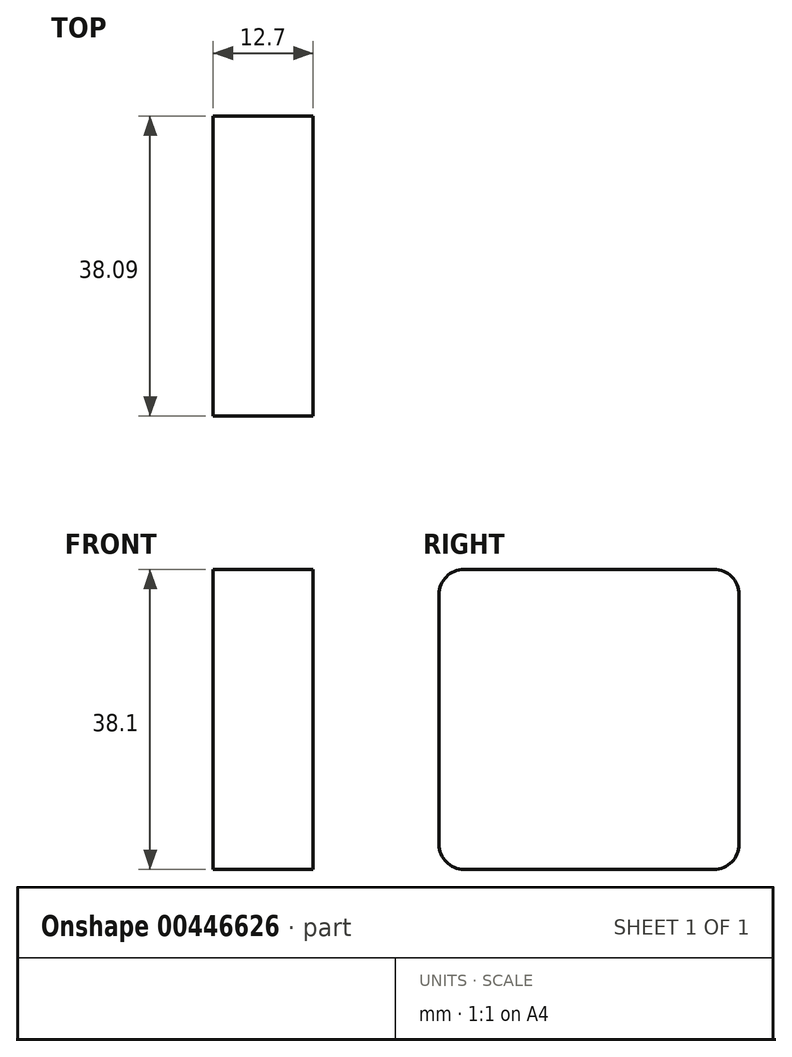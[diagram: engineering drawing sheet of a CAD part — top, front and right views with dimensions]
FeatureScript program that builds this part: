
annotation { "Feature Type Name" : "Feature", "Feature Type Description" : "" }
export const myFeature = defineFeature(function(context is Context, id is Id, definition is map)
    precondition{}
    {
        {
            var Q0;
            Q0=qCreatedBy(makeId("Right.planeOp"),FACE);
            var sketch = newSketch(context, id + "F0", { "sketchPlane" : qUnion([Q0])});
            skLineSegment(sketch, "E0.0", {"start": v(34.93, 0) * mm, "end": v(34.93, 31.75) * mm});
            skLineSegment(sketch, "E0.1", {"start": v(0, -3.17) * mm, "end": v(31.75, -3.17) * mm});
            skLineSegment(sketch, "E0.2", {"start": v(-3.18, 0) * mm, "end": v(-3.18, 31.75) * mm});
            skLineSegment(sketch, "E0.3", {"start": v(0, 34.93) * mm, "end": v(31.75, 34.93) * mm});
            skPoint(sketch, "E1.visualSharp", {"position": v(34.93, 34.93) * mm});
            skArc(sketch, "E1.filletArc", {"start": v(34.93, 31.75) * mm, "mid": v(34, 34) * mm, "end": v(31.75, 34.92) * mm});
            skPoint(sketch, "E2.visualSharp", {"position": v(34.93, -3.17) * mm});
            skArc(sketch, "E2.filletArc", {"start": v(31.75, -3.18) * mm, "mid": v(34, -2.25) * mm, "end": v(34.93, 0) * mm});
            skPoint(sketch, "E3.visualSharp", {"position": v(-3.17, -3.17) * mm});
            skArc(sketch, "E3.filletArc", {"start": v(-3.17, 0) * mm, "mid": v(-2.25, -2.25) * mm, "end": v(0, -3.17) * mm});
            skPoint(sketch, "E4.visualSharp", {"position": v(-3.17, 34.93) * mm});
            skArc(sketch, "E4.filletArc", {"start": v(0, 34.93) * mm, "mid": v(-2.25, 34) * mm, "end": v(-3.17, 31.75) * mm});
            skSolve(sketch);
        }
        {
            var Q0;
            Q0=makeQuery(id+"F0.imprint","IMPRINT",FACE,{"disambiguationData":[TD([[makeQuery(id+"F0.imprint","IMPRINT",EDGE,{"derivedFrom":sQuery(id+"F0.wireOp",EDGE,"E0.0")}),1.0]])]});
            extrude(context, id + "F1", {"entities" : qUnion([Q0]), "depth" : 12.7 * mm});
        }
        {
            var Q0;
            Q0=makeQuery(id+"F1.opExtrude","CAP_FACE",FACE,{"disambiguationData":[OSD([sQuery(id+"F0.wireOp",EDGE,"3f405e9c-8b5e-4db3-a756-02e33879b2d6.bottom"),sQuery(id+"F0.wireOp",EDGE,"3f405e9c-8b5e-4db3-a756-02e33879b2d6.top"),sQuery(id+"F0.wireOp",EDGE,"3f405e9c-8b5e-4db3-a756-02e33879b2d6.left"),sQuery(id+"F0.wireOp",EDGE,"3f405e9c-8b5e-4db3-a756-02e33879b2d6.right"),sQuery(id+"F0.wireOp",EDGE,"E0.0"),sQuery(id+"F0.wireOp",EDGE,"E0.1"),sQuery(id+"F0.wireOp",EDGE,"E0.2"),sQuery(id+"F0.wireOp",EDGE,"E0.3"),sQuery(id+"F0.wireOp",EDGE,"E1.filletArc"),sQuery(id+"F0.wireOp",EDGE,"E2.filletArc"),sQuery(id+"F0.wireOp",EDGE,"E3.filletArc"),sQuery(id+"F0.wireOp",EDGE,"E4.filletArc")])],"isStart":false});
            cPlane(context, id + "F2", {"entities" : qUnion([Q0]), "cplaneType" : CPlaneType.OFFSET, "offset" : 25.4 * mm, "width" : 152.4 * mm, "height" : 152.4 * mm});
        }
    });
